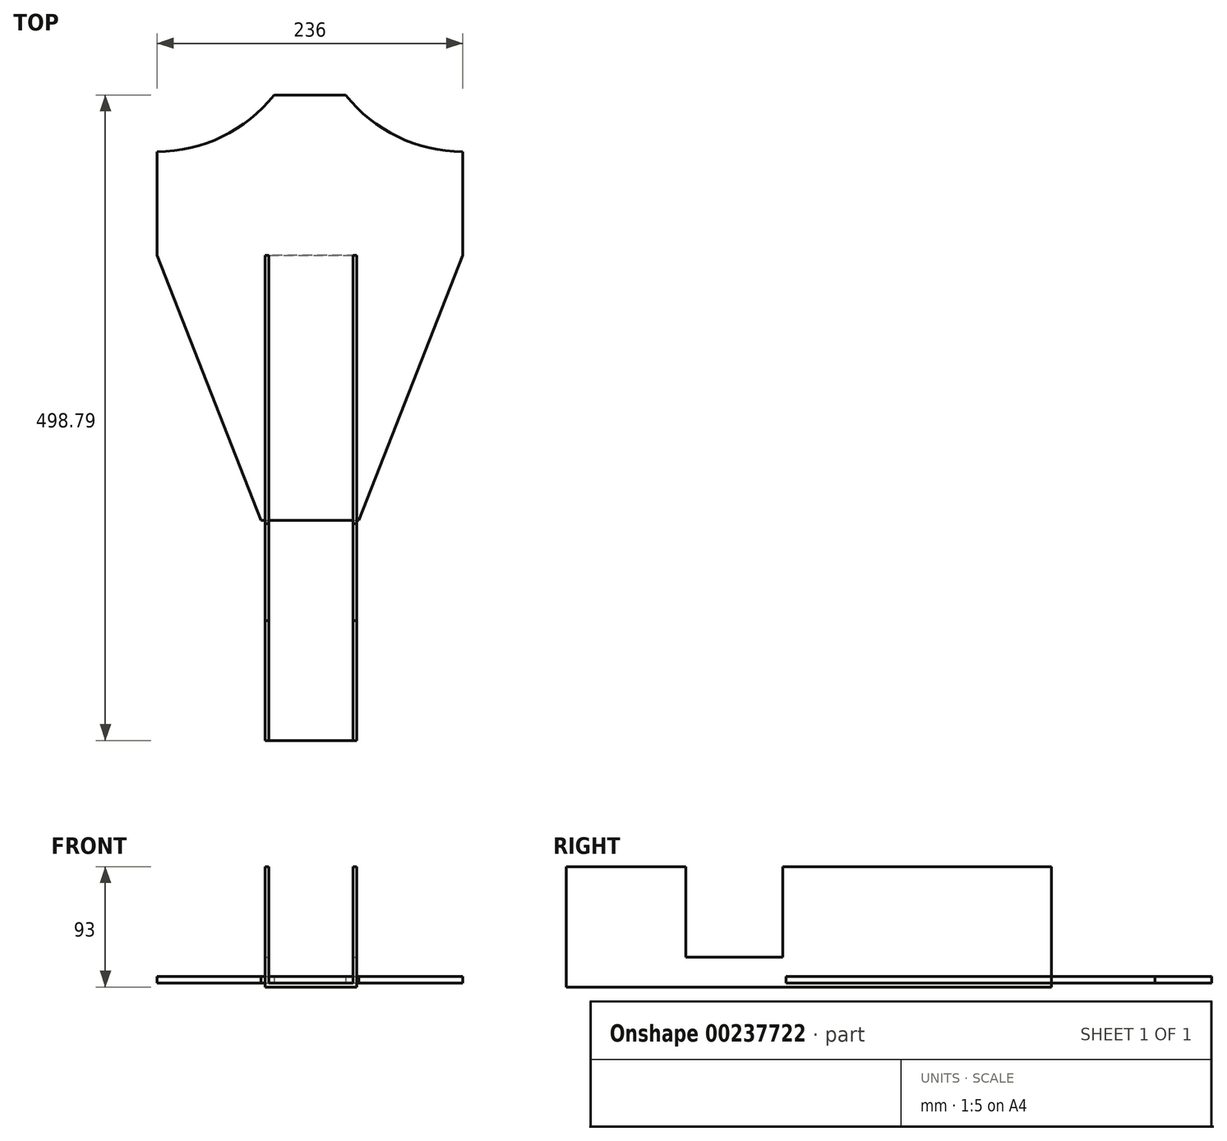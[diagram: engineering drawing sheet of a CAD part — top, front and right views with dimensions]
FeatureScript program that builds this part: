
annotation { "Feature Type Name" : "Feature", "Feature Type Description" : "" }
export const myFeature = defineFeature(function(context is Context, id is Id, definition is map)
    precondition{}
    {
        {
            var Q0;
            Q0=qCreatedBy(makeId("Front.planeOp"),FACE);
            var sketch = newSketch(context, id + "F0", { "sketchPlane" : qUnion([Q0])});
            skLineSegment(sketch, "E0", {"start": v(-31.75, 90) * mm, "end": v(-31.75, 0) * mm});
            skLineSegment(sketch, "E1", {"start": v(-31.75, 0) * mm, "end": v(33.25, 0) * mm});
            skLineSegment(sketch, "E2", {"start": v(33.25, 0) * mm, "end": v(33.25, 90) * mm});
            skLineSegment(sketch, "E3", {"start": v(33.25, 90) * mm, "end": v(36.25, 90) * mm});
            skLineSegment(sketch, "E4", {"start": v(36.25, 90) * mm, "end": v(36.25, -3) * mm});
            skLineSegment(sketch, "E5", {"start": v(36.25, -3) * mm, "end": v(-34.75, -3) * mm});
            skLineSegment(sketch, "E6", {"start": v(-34.75, -3) * mm, "end": v(-34.75, 90) * mm});
            skLineSegment(sketch, "E7", {"start": v(-34.75, 90) * mm, "end": v(-31.75, 90) * mm});
            skSolve(sketch);
        }
        {
            var Q0;
            Q0=qSketchRegion(id+"F0",true);
            extrude(context, id + "F1", {"entities" : qUnion([Q0]), "depth" : 375 * mm});
        }
        {
            var Q0;
            Q0=makeQuery(id+"F1.opExtrude","SWEPT_FACE",FACE,{"disambiguationData":[OSD([sQuery(id+"F0.wireOp",EDGE,"E4")])]});
            var sketch = newSketch(context, id + "F2", { "sketchPlane" : qUnion([Q0])});
            skLineSegment(sketch, "E8.bottom", {"start": v(-282.5, 90) * mm, "end": v(-207.5, 90) * mm});
            skLineSegment(sketch, "E8.top", {"start": v(-282.5, 20) * mm, "end": v(-207.5, 20) * mm});
            skLineSegment(sketch, "E8.left", {"start": v(-282.5, 90) * mm, "end": v(-282.5, 20) * mm});
            skLineSegment(sketch, "E8.right", {"start": v(-207.5, 90) * mm, "end": v(-207.5, 20) * mm});
            skSolve(sketch);
        }
        {
            var Q0;
            Q0=qSketchRegion(id+"F2",true);
            extrude(context, id + "F3", {"entities" : qUnion([Q0]), "operationType" : NewBodyOperationType.REMOVE, "oppositeDirection" : true, "depth" : 107 * mm});
        }
        {
            var Q0;
            Q0=qCreatedBy(makeId("Top.planeOp"),FACE);
            var sketch = newSketch(context, id + "F4", { "sketchPlane" : qUnion([Q0])});
            skLineSegment(sketch, "E9.bottom", {"start": v(-118, 0) * mm, "end": v(118, 0) * mm});
            skLineSegment(sketch, "E9.top", {"start": v(-37.7, -205) * mm, "end": v(37.7, -205) * mm});
            skLineSegment(sketch, "E10.left", {"start": v(-118, 0) * mm, "end": v(-118, 80) * mm});
            skLineSegment(sketch, "E10.right", {"start": v(118, 0) * mm, "end": v(118, 80) * mm});
            skArc(sketch, "E11", {"start": v(-118, 80) * mm, "mid": v(-67.82, 91.52) * mm, "end": v(-27.7, 123.79) * mm});
            skArc(sketch, "E12", {"start": v(27.7, 123.79) * mm, "mid": v(67.82, 91.52) * mm, "end": v(118, 80) * mm});
            skLineSegment(sketch, "E13", {"start": v(-27.7, 123.79) * mm, "end": v(-27.7, -205) * mm, "construction": true});
            skLineSegment(sketch, "E14", {"start": v(27.7, 0) * mm, "end": v(27.7, -205) * mm, "construction": true});
            skLineSegment(sketch, "E15", {"start": v(-27.7, 123.79) * mm, "end": v(27.7, 123.79) * mm});
            skLineSegment(sketch, "E16.trimOffspring", {"start": v(-118, 195) * mm, "end": v(-118, 195.81) * mm});
            skPoint(sketch, "E17.orphan", {"position": v(-27.7, 0) * mm});
            skLineSegment(sketch, "E18", {"start": v(-37.7, -205) * mm, "end": v(-118, 0) * mm});
            skLineSegment(sketch, "E19", {"start": v(37.7, -205) * mm, "end": v(118, 0) * mm});
            skLineSegment(sketch, "E20.trimOffspring", {"start": v(118, 195) * mm, "end": v(118, 195.81) * mm});
            skSolve(sketch);
        }
        {
            var Q0;
            Q0=qSketchRegion(id+"F4",true);
            extrude(context, id + "F5", {"entities" : qUnion([Q0]), "depth" : 5 * mm});
        }
    });
